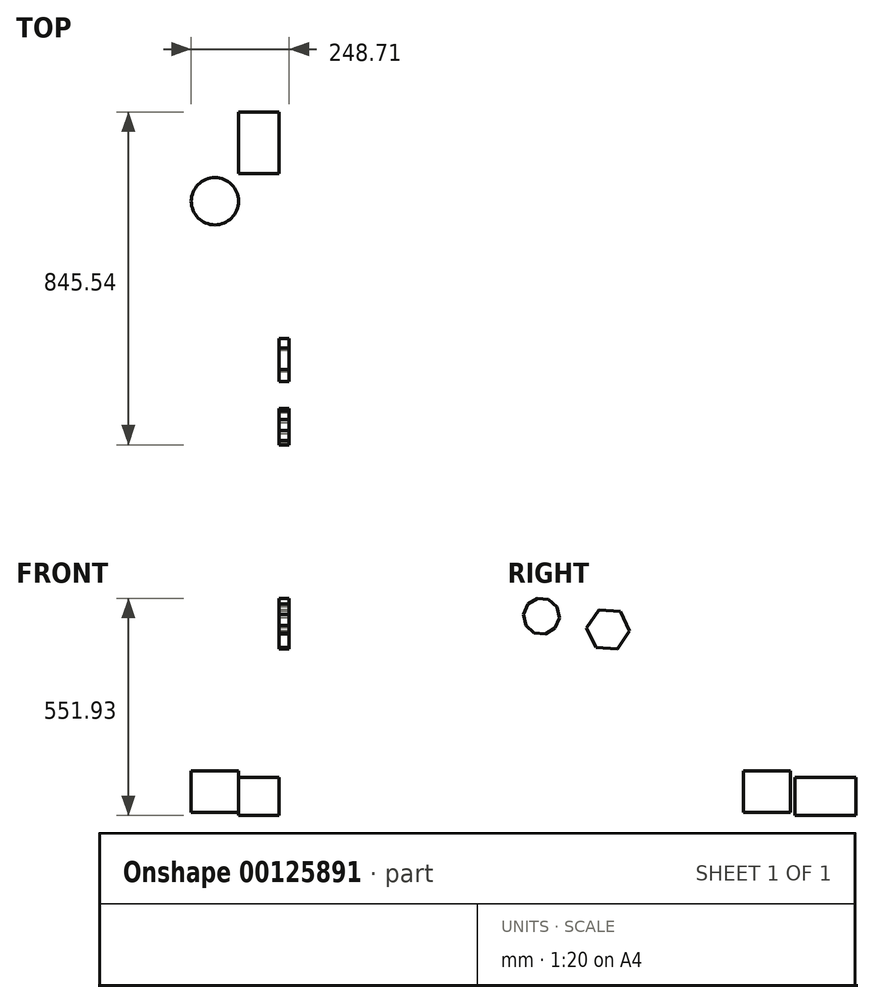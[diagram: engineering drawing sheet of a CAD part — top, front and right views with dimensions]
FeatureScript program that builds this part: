
annotation { "Feature Type Name" : "Feature", "Feature Type Description" : "" }
export const myFeature = defineFeature(function(context is Context, id is Id, definition is map)
    precondition{}
    {
        {
            var Q0;
            Q0=qCreatedBy(makeId("Front.planeOp"),FACE);
            var sketch = newSketch(context, id + "F0", { "sketchPlane" : qUnion([Q0])});
            skLineSegment(sketch, "E0.bottom", {"start": v(-72.73, -16.47) * mm, "end": v(30.4, -16.47) * mm});
            skLineSegment(sketch, "E0.top", {"start": v(-72.73, -113.71) * mm, "end": v(30.4, -113.71) * mm});
            skLineSegment(sketch, "E0.left", {"start": v(-72.73, -16.47) * mm, "end": v(-72.73, -113.71) * mm});
            skLineSegment(sketch, "E0.right", {"start": v(30.4, -16.47) * mm, "end": v(30.4, -113.71) * mm});
            skSolve(sketch);
        }
        {
            var Q0;
            Q0 = qSketchRegion(id + "F0", true);
            extrude(context, id + "F1", {"entities" : qUnion([Q0]), "oppositeDirection" : true, "depth" : 156.05 * mm});
        }
        {
            var Q0;
            Q0=qCreatedBy(makeId("Top.planeOp"),FACE);
            var sketch = newSketch(context, id + "F2", { "sketchPlane" : qUnion([Q0])});
            skCircle(sketch, "E1", {"center": v(-132.93, -70.6) * mm, "radius": 59.98 * mm});
            skSolve(sketch);
        }
        {
            var Q0;
            Q0 = qSketchRegion(id + "F2", true);
            extrude(context, id + "F3", {"entities" : qUnion([Q0]), "oppositeDirection" : true, "depth" : 105.6 * mm});
        }
        {
            var Q0;
            Q0=makeQuery(id+"F1.opExtrude","SWEPT_FACE",FACE,{"disambiguationData":[OSD([sQuery(id+"F0.wireOp",EDGE,"E0.right")])]});
            var sketch = newSketch(context, id + "F4", { "sketchPlane" : qUnion([Q0])});
            skCircle(sketch, "E2.cCircle", {"center": v(-474.02, 359.28) * mm, "radius": 47.48 * mm, "construction": true});
            skLineSegment(sketch, "E2.0", {"start": v(-528.68, 363.45) * mm, "end": v(-497.74, 408.7) * mm});
            skLineSegment(sketch, "E2.1", {"start": v(-497.74, 408.7) * mm, "end": v(-443.07, 404.54) * mm});
            skLineSegment(sketch, "E2.2", {"start": v(-443.07, 404.54) * mm, "end": v(-419.35, 355.11) * mm});
            skLineSegment(sketch, "E2.3", {"start": v(-419.35, 355.11) * mm, "end": v(-450.3, 309.85) * mm});
            skLineSegment(sketch, "E2.4", {"start": v(-450.3, 309.85) * mm, "end": v(-504.96, 314.02) * mm});
            skLineSegment(sketch, "E2.5", {"start": v(-504.96, 314.02) * mm, "end": v(-528.68, 363.45) * mm});
            skPoint(sketch, "E2.0.midPoint", {"position": v(-513.21, 386.08) * mm});
            skCircle(sketch, "E3.cCircle", {"center": v(-643.51, 393.1) * mm, "radius": 43.93 * mm, "construction": true});
            skLineSegment(sketch, "E3.0", {"start": v(-608.94, 362.46) * mm, "end": v(-633.56, 348) * mm});
            skLineSegment(sketch, "E3.1", {"start": v(-633.56, 348) * mm, "end": v(-661.97, 350.76) * mm});
            skLineSegment(sketch, "E3.2", {"start": v(-661.97, 350.76) * mm, "end": v(-683.34, 369.7) * mm});
            skLineSegment(sketch, "E3.3", {"start": v(-683.34, 369.7) * mm, "end": v(-689.5, 397.58) * mm});
            skLineSegment(sketch, "E3.4", {"start": v(-689.5, 397.58) * mm, "end": v(-678.08, 423.75) * mm});
            skLineSegment(sketch, "E3.5", {"start": v(-678.08, 423.75) * mm, "end": v(-653.47, 438.22) * mm});
            skLineSegment(sketch, "E3.6", {"start": v(-653.47, 438.22) * mm, "end": v(-625.05, 435.45) * mm});
            skLineSegment(sketch, "E3.7", {"start": v(-625.05, 435.45) * mm, "end": v(-603.69, 416.51) * mm});
            skLineSegment(sketch, "E3.8", {"start": v(-603.69, 416.51) * mm, "end": v(-597.53, 388.64) * mm});
            skLineSegment(sketch, "E3.9", {"start": v(-597.53, 388.64) * mm, "end": v(-608.94, 362.46) * mm});
            skPoint(sketch, "E3.0.midPoint", {"position": v(-621.25, 355.23) * mm});
            skSolve(sketch);
        }
        {
            var Q0;
            Q0 = qSketchRegion(id + "F4", true);
            extrude(context, id + "F5", {"entities" : qUnion([Q0]), "depth" : 25.4 * mm});
        }
    });
